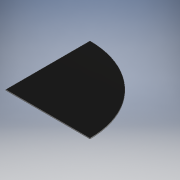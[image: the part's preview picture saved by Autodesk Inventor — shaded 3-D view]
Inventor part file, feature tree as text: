
AUTODESK INVENTOR PART (.ipt)
format: ipt  version: 2016 (Build 200138000, 138)  size: 92,160 bytes
history: native  units: mm
features: extrude x1, sketch x1
ambient origin geometry x8: Origin, YZ Plane, XZ Plane, XY Plane, X Axis, Y Axis, Z Axis, Center Point
bodies: 实体1 (feature_tree)
feature tree (2):
  extrude  "拉伸1"  Depth=500.0mm
  sketch  "草图1"  dims[d0=500.0mm d1=500.0mm d2=90.0deg d3=500.0mm d4=5.0mm d5=0.0mm]
